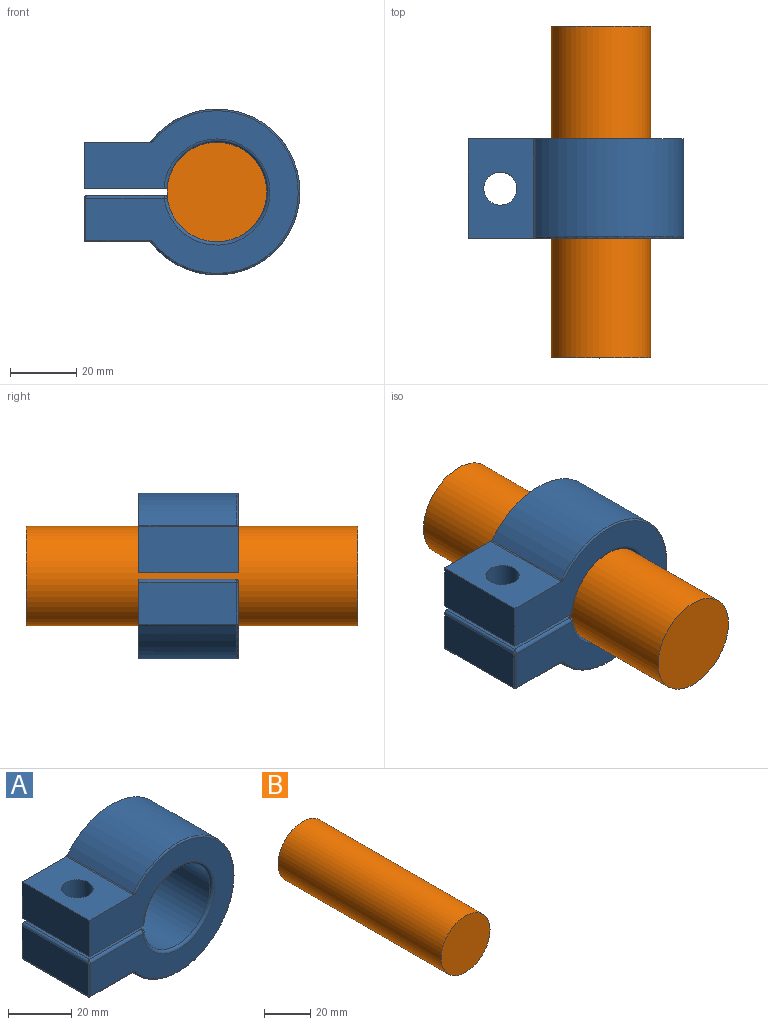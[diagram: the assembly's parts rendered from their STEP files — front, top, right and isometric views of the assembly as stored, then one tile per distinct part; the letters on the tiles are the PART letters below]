
ASSEMBLY  parts=2 mates=1
PART A: 26 faces, bbox 67.3x30.8x54.4 mm
  f0: plane 30.03x25.06mm, normal (0,0,-1), area 672.2mm2, adj f1,f7,f8,f9,f11,f20
  f1: cylinder r=15mm len=30mm, axis (0,1,0), area 2649.6mm2, adj f0,f9,f20,f22
  f2: plane 29x23.13mm, normal (0,0,1), area 592.1mm2, adj f9,f10,f17,f19,f22
  f3: plane 29.5x12.5mm, normal (-1,0,0), area 368.7mm2, adj f9,f14,f16,f19
  f4: plane 29.51x19.51mm, normal (0,0,-1), area 496.7mm2, adj f5,f9,f10,f13,f16,f23
  f5: cylinder r=25mm len=50mm, axis (0,1,0), area 3677.4mm2, adj f4,f9,f12,f23,f24
  f6: plane 30x19.92mm, normal (0,0,1), area 514mm2, adj f7,f8,f9,f11,f24,f25
  f7: plane 30x14mm, normal (-1,0,0), area 420mm2, adj f0,f6,f8,f9
  f8: plane 64.78x49.28mm, normal (0,-1,0), area 1507mm2, adj f0,f6,f7,f12,f13,f14,f17,f20
  f9: plane 65x50mm, normal (0,1,0), area 1704mm2, adj f0,f1,f2,f3,f4,f5,f6,f7
  f10: cylinder r=5mm len=14mm, axis (0,0,1), area 439.8mm2, adj f2,f4
  f11: cylinder r=5mm len=14mm, axis (0,0,1), area 439.8mm2, adj f0,f6
  f12: torus R=24.5mm, axis (0,-1,0), area 96.9mm2, adj f5,f8,f23,f25
  f13: cylinder r=0.5mm len=19.75mm, axis (-1,0,0), area 15.3mm2, adj f4,f8,f15,f23
  f14: cylinder r=0.5mm len=12.5mm, axis (0,0,1), area 9.8mm2, adj f3,f8,f15,f18
  f15: sphere r=0.5mm, area 0.4mm2, adj f13,f14,f16
  f16: cylinder r=0.5mm len=29.5mm, axis (0,1,0), area 23.2mm2, adj f3,f4,f9,f15
  f17: cylinder r=1mm len=23.63mm, axis (1,0,0), area 36.7mm2, adj f2,f8,f18,f21
  f18: bspline ~1.05x1mm, area 0.5mm2, adj f14,f17,f19
  f19: cylinder r=1mm len=29.5mm, axis (0,1,0), area 45.9mm2, adj f2,f3,f9,f18
  f20: torus R=16mm, axis (0,-1,0), area 147mm2, adj f0,f1,f8,f21
  f21: sphere r=1mm, area 1.5mm2, adj f17,f20,f22
  f22: cylinder r=1mm len=29mm, axis (0,1,0), area 41.9mm2, adj f1,f2,f9,f21
  f23: bspline ~0.79x0.7mm, area 0.2mm2, adj f4,f5,f12,f13
  f24: cylinder r=0.5mm len=29.5mm, axis (0,1,0), area 13.5mm2, adj f5,f6,f9,f25
  f25: bspline ~1.62x1.05mm, area 0.5mm2, adj f6,f8,f12,f24
PART B: 3 faces, bbox 30x100x30 mm
  f0: cylinder r=15mm len=100mm, axis (0,1,0), area 9424.8mm2, adj f1,f2
  f1: plane 30x30mm, normal (0,-1,0), area 706.9mm2, adj f0
  f2: plane 30x30mm, normal (0,1,0), area 706.9mm2, adj f0
PLACE A t=(-26.4,-6.24,-2.5)mm
PLACE B t=(-26.4,27.76,-2.5)mm
MATE cylindrical B.f0 <-> A.f1  axis (0,1,0) through (-26.4,-22.24,-2.5)mm
